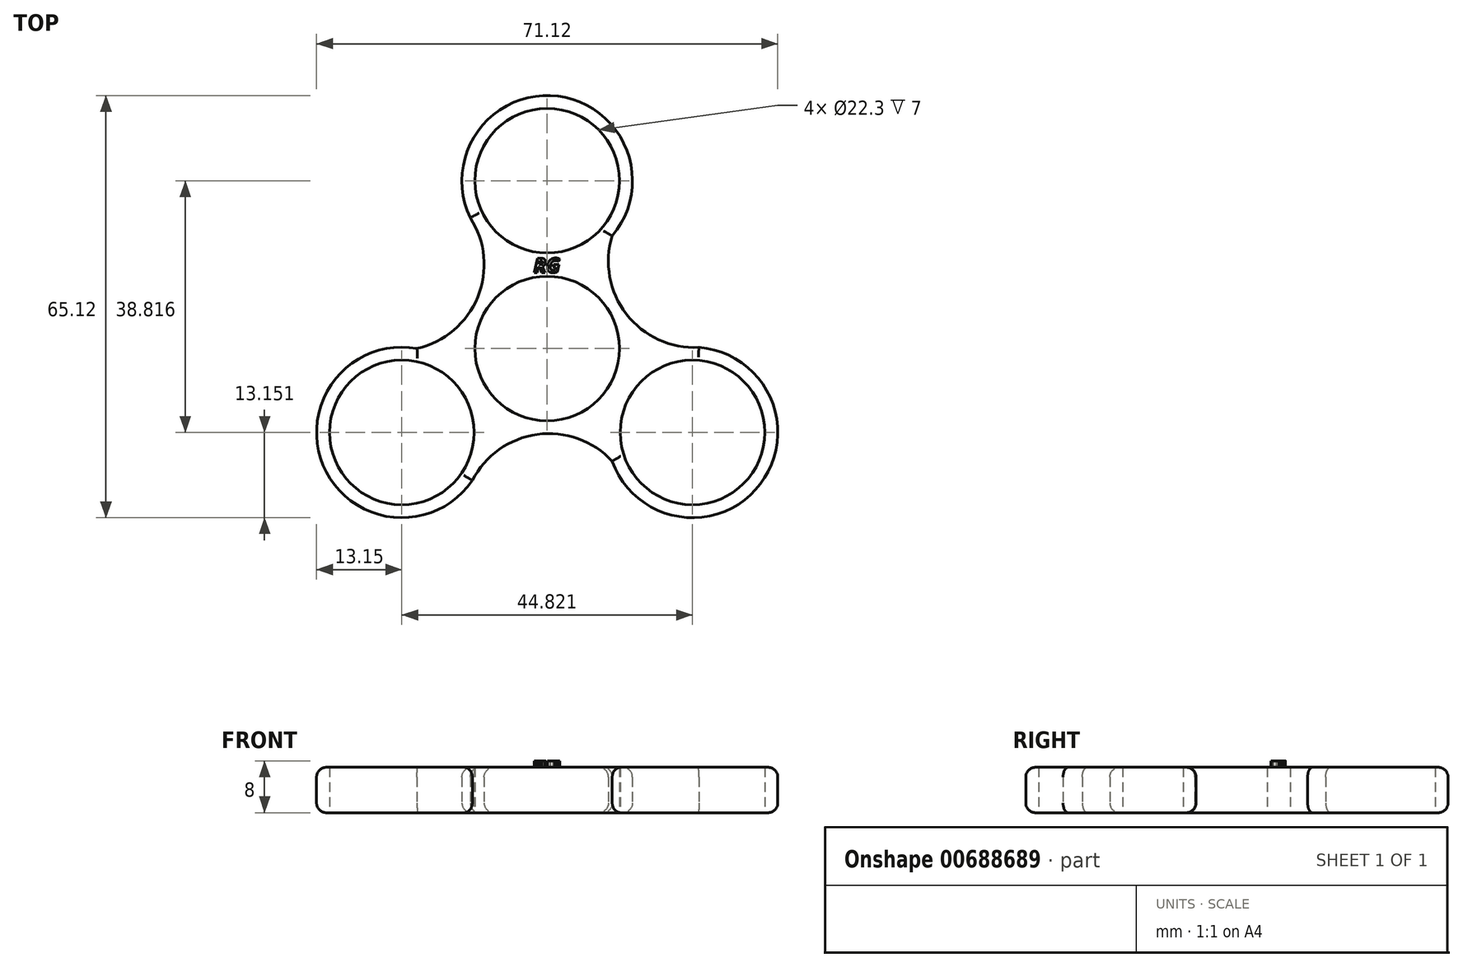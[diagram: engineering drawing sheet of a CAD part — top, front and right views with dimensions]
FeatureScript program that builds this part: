
annotation { "Feature Type Name" : "Feature", "Feature Type Description" : "" }
export const myFeature = defineFeature(function(context is Context, id is Id, definition is map)
    precondition{}
    {
        {
            var Q0;
            Q0=qCreatedBy(makeId("Top.planeOp"),FACE);
            var sketch = newSketch(context, id + "F0", { "sketchPlane" : qUnion([Q0])});
            skCircle(sketch, "E0", {"center": v(0, 0) * mm, "radius": 11.15 * mm});
            skArc(sketch, "E1", {"start": v(-11.14, 6.98) * mm, "mid": v(-11.46, 6.45) * mm, "end": v(-11.75, 5.9) * mm});
            skCircle(sketch, "E2", {"center": v(0, 25.88) * mm, "radius": 11.15 * mm});
            skArc(sketch, "E3.1.0", {"start": v(-20.06, 0) * mm, "mid": v(-34.2, -18.76) * mm, "end": v(-10.71, -18.94) * mm});
            skCircle(sketch, "E3.1.1", {"center": v(-22.41, -12.94) * mm, "radius": 11.15 * mm});
            skCircle(sketch, "E3.2.1", {"center": v(22.41, -12.94) * mm, "radius": 11.15 * mm});
            skArc(sketch, "E4", {"start": v(-20.06, 0) * mm, "mid": v(-10.7, 7.94) * mm, "end": v(-11.84, 20.16) * mm});
            skArc(sketch, "E5.1.0", {"start": v(10.03, -17.37) * mm, "mid": v(-1.52, -13.24) * mm, "end": v(-11.54, -20.34) * mm});
            skArc(sketch, "E5.2.0", {"start": v(10.03, 17.37) * mm, "mid": v(12.23, 5.3) * mm, "end": v(23.38, 0.18) * mm});
            skArc(sketch, "E6.trimOffspring", {"start": v(11.62, 6.16) * mm, "mid": v(11.32, 6.7) * mm, "end": v(11, 7.22) * mm});
            skArc(sketch, "E7.trimOffspring", {"start": v(-0.47, -13.14) * mm, "mid": v(0.14, -13.15) * mm, "end": v(0.76, -13.13) * mm});
            skArc(sketch, "E8.trimOffspring", {"start": v(10.03, 17.37) * mm, "mid": v(0.85, 39) * mm, "end": v(-11.05, 18.75) * mm});
            skArc(sketch, "E9.trimOffspring", {"start": v(10.03, -17.37) * mm, "mid": v(33.35, -20.24) * mm, "end": v(21.76, 0.2) * mm});
            skSolve(sketch);
        }
        {
            var Q0;
            Q0=makeQuery(id+"F0.imprint","IMPRINT",FACE,{"disambiguationData":[TD([[makeQuery(id+"F0.imprint","IMPRINT",EDGE,{"derivedFrom":sQuery(id+"F0.wireOp",EDGE,"E0")}),-1.0]])]});
            extrude(context, id + "F1", {"entities" : qUnion([Q0]), "depth" : 7 * mm, "offsetDistance" : 25 * mm});
        }
        {
            var Q0;
            Q0=makeQuery(id+"F1.opExtrude","CAP_EDGE",EDGE,{"disambiguationData":[OSD([sQuery(id+"F0.wireOp",EDGE,"E3.1.0")])],"isStart":false});
            var Q1;
            Q1=makeQuery(id+"F1.opExtrude","CAP_EDGE",EDGE,{"disambiguationData":[OSD([sQuery(id+"F0.wireOp",EDGE,"E4")])],"isStart":false});
            var Q2;
            Q2=makeQuery(id+"F1.opExtrude","CAP_EDGE",EDGE,{"disambiguationData":[OSD([sQuery(id+"F0.wireOp",EDGE,"E8.trimOffspring")])],"isStart":false});
            var Q3;
            Q3=makeQuery(id+"F1.opExtrude","CAP_EDGE",EDGE,{"disambiguationData":[OSD([sQuery(id+"F0.wireOp",EDGE,"E5.2.0")])],"isStart":false});
            var Q4;
            Q4=makeQuery(id+"F1.opExtrude","CAP_EDGE",EDGE,{"disambiguationData":[OSD([sQuery(id+"F0.wireOp",EDGE,"E9.trimOffspring")])],"isStart":false});
            var Q5;
            Q5=makeQuery(id+"F1.opExtrude","CAP_EDGE",EDGE,{"disambiguationData":[OSD([sQuery(id+"F0.wireOp",EDGE,"E5.1.0")])],"isStart":false});
            var Q6;
            Q6=makeQuery(id+"F1.opExtrude","CAP_EDGE",EDGE,{"disambiguationData":[OSD([sQuery(id+"F0.wireOp",EDGE,"E8.trimOffspring")])],"isStart":true});
            var Q7;
            Q7=makeQuery(id+"F1.opExtrude","CAP_EDGE",EDGE,{"disambiguationData":[OSD([sQuery(id+"F0.wireOp",EDGE,"E5.2.0")])],"isStart":true});
            var Q8;
            Q8=makeQuery(id+"F1.opExtrude","CAP_EDGE",EDGE,{"disambiguationData":[OSD([sQuery(id+"F0.wireOp",EDGE,"E9.trimOffspring")])],"isStart":true});
            var Q9;
            Q9=makeQuery(id+"F1.opExtrude","CAP_EDGE",EDGE,{"disambiguationData":[OSD([sQuery(id+"F0.wireOp",EDGE,"E5.1.0")])],"isStart":true});
            var Q10;
            Q10=makeQuery(id+"F1.opExtrude","CAP_EDGE",EDGE,{"disambiguationData":[OSD([sQuery(id+"F0.wireOp",EDGE,"E3.1.0")])],"isStart":true});
            var Q11;
            Q11=makeQuery(id+"F1.opExtrude","CAP_EDGE",EDGE,{"disambiguationData":[OSD([sQuery(id+"F0.wireOp",EDGE,"E4")])],"isStart":true});
            fillet(context, id + "F2", {"entities" : qUnion([Q0, Q1, Q2, Q3, Q4, Q5, Q6, Q7, Q8, Q9, Q10, Q11]), "radius" : 1.5 * mm, "tangentPropagation" : true, "allowEdgeOverflow" : false});
        }
        {
            var Q0;
            Q0=makeQuery(id+"F1.opExtrude","CAP_FACE",FACE,{"disambiguationData":[OSD([sQuery(id+"F0.wireOp",EDGE,"E0"),sQuery(id+"F0.wireOp",EDGE,"E2"),sQuery(id+"F0.wireOp",EDGE,"E3.1.0"),sQuery(id+"F0.wireOp",EDGE,"E3.1.1"),sQuery(id+"F0.wireOp",EDGE,"E3.2.1"),sQuery(id+"F0.wireOp",EDGE,"E4"),sQuery(id+"F0.wireOp",EDGE,"E5.1.0"),sQuery(id+"F0.wireOp",EDGE,"E5.2.0"),sQuery(id+"F0.wireOp",EDGE,"E8.trimOffspring"),sQuery(id+"F0.wireOp",EDGE,"E9.trimOffspring")])],"isStart":false});
            var sketch = newSketch(context, id + "F3", { "sketchPlane" : qUnion([Q0])});
            skText(sketch, "E10", { "text": "RG", "fontName": "OpenSans-BoldItalic.ttf"});
            const initialGuessF3  = {"E10": [-0.00206, 0.01172, 1, 0, 0.00223]};
            skSetInitialGuess(sketch, initialGuessF3);
            skSolve(sketch);
        }
        {
            var Q0;
            Q0 = qSketchRegion(id + "F3", true);
            extrude(context, id + "F4", {"entities" : qUnion([Q0]), "operationType" : NewBodyOperationType.ADD, "depth" : 1 * mm, "offsetDistance" : 25 * mm});
        }
    });
